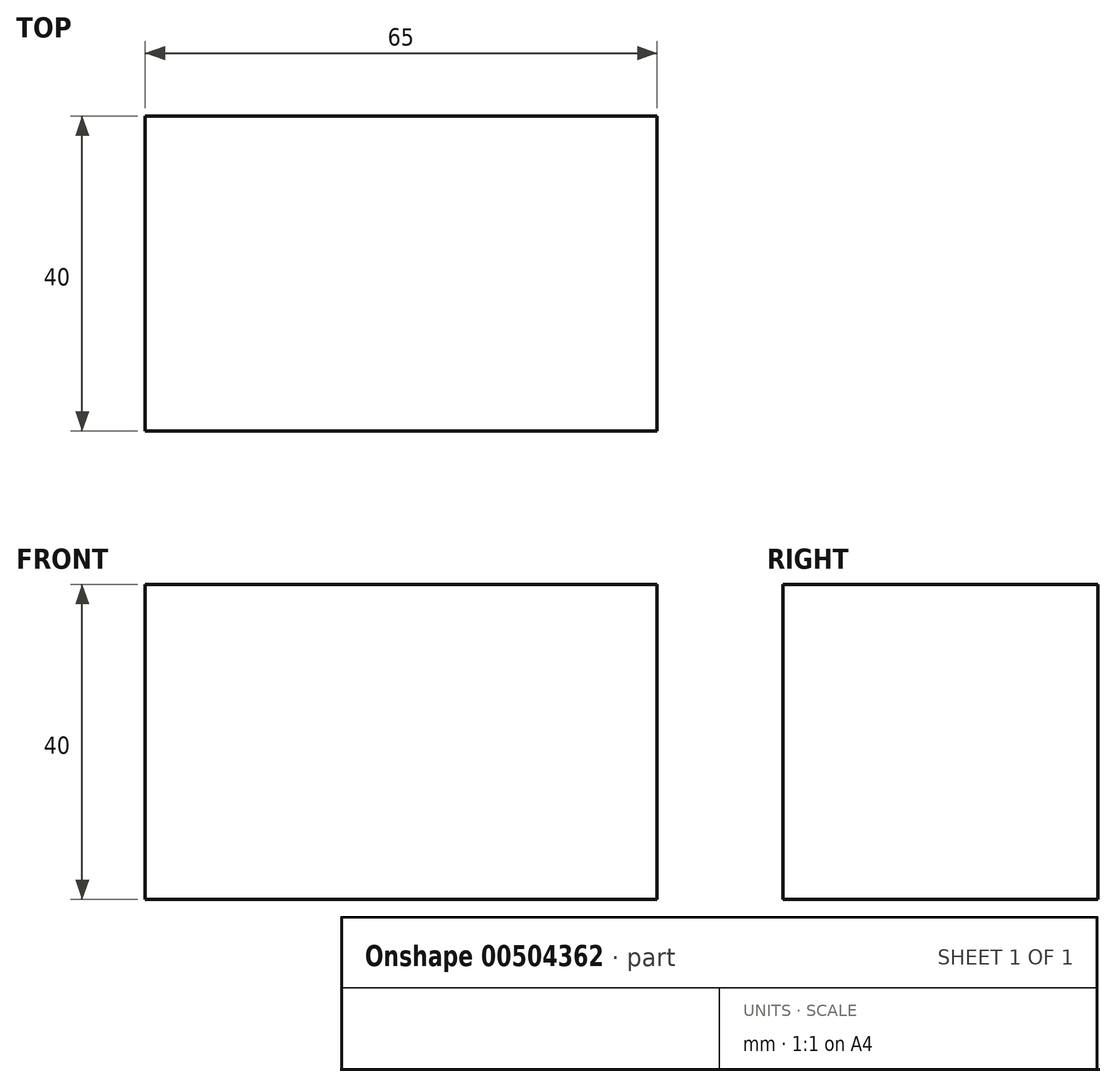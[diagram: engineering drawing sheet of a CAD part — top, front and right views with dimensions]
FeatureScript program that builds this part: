
annotation { "Feature Type Name" : "Feature", "Feature Type Description" : "" }
export const myFeature = defineFeature(function(context is Context, id is Id, definition is map)
    precondition{}
    {
        {
            var Q0;
            Q0=qCreatedBy(makeId("Front.planeOp"),FACE);
            var sketch = newSketch(context, id + "F0", { "sketchPlane" : qUnion([Q0])});
            skLineSegment(sketch, "E0.bottom", {"start": v(-31.96, 18.95) * mm, "end": v(33.04, 18.95) * mm});
            skLineSegment(sketch, "E0.top", {"start": v(-31.96, -21.05) * mm, "end": v(33.04, -21.05) * mm});
            skLineSegment(sketch, "E0.left", {"start": v(-31.96, 18.95) * mm, "end": v(-31.96, -21.05) * mm});
            skLineSegment(sketch, "E0.right", {"start": v(33.04, 18.95) * mm, "end": v(33.04, -21.05) * mm});
            skSolve(sketch);
        }
        {
            var Q0;
            Q0=makeQuery(id+"F0.imprint","IMPRINT",FACE,{"disambiguationData":[TD([[makeQuery(id+"F0.imprint","IMPRINT",EDGE,{"derivedFrom":sQuery(id+"F0.wireOp",EDGE,"E0.bottom")}),-1.0]])]});
            extrude(context, id + "F1", {"entities" : qUnion([Q0]), "depth" : 40 * mm});
        }
    });
